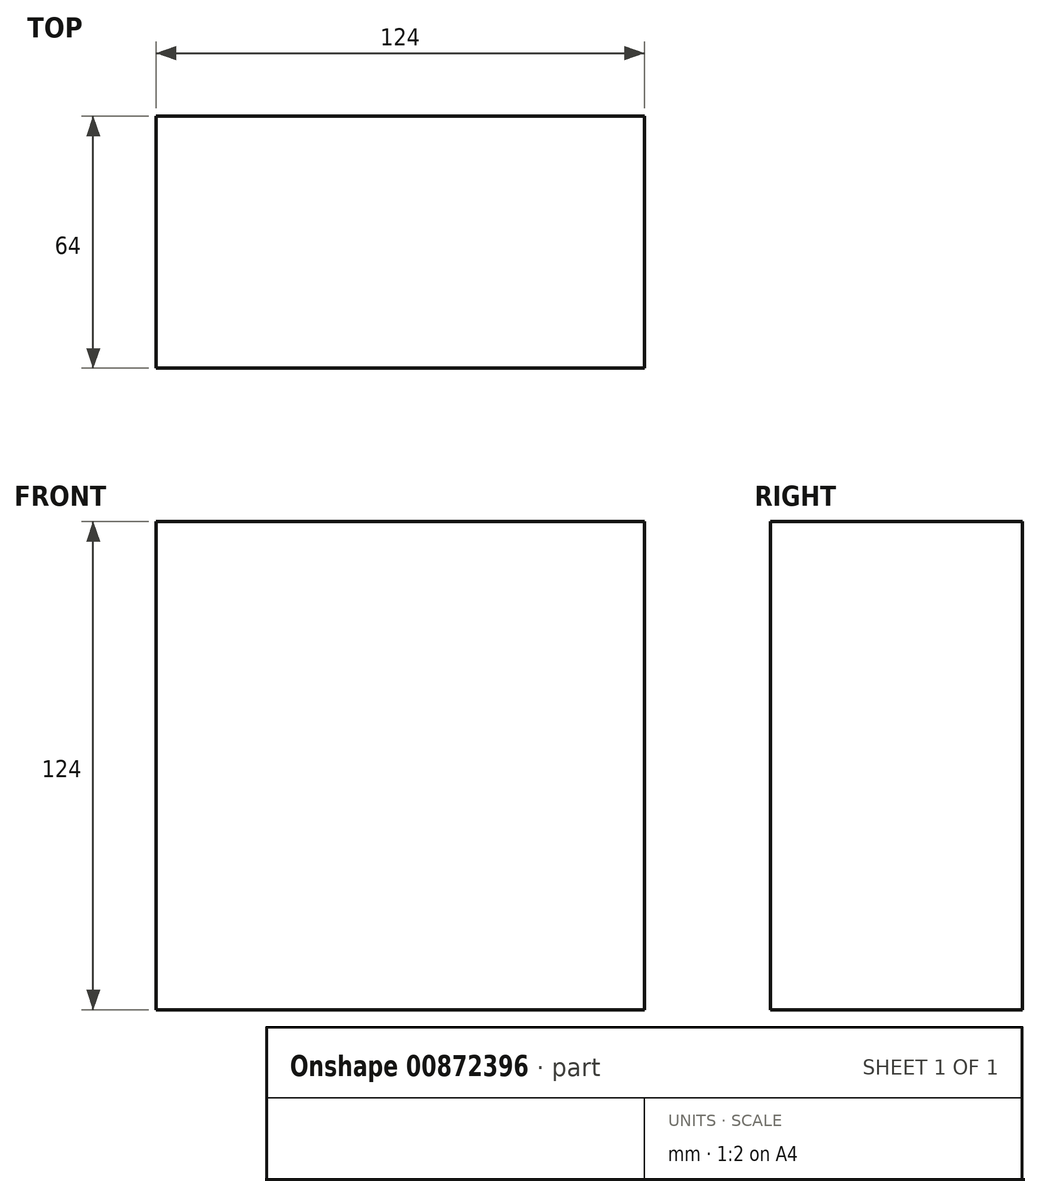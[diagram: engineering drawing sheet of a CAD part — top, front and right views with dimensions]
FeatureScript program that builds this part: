
annotation { "Feature Type Name" : "Feature", "Feature Type Description" : "" }
export const myFeature = defineFeature(function(context is Context, id is Id, definition is map)
    precondition{}
    {
        {
            var Q0;
            Q0=qCreatedBy(makeId("Top.planeOp"),FACE);
            var sketch = newSketch(context, id + "F0", { "sketchPlane" : qUnion([Q0])});
            skLineSegment(sketch, "E0.bottom", {"start": v(-62, 32) * mm, "end": v(62, 32) * mm});
            skLineSegment(sketch, "E0.top", {"start": v(-62, -32) * mm, "end": v(62, -32) * mm});
            skLineSegment(sketch, "E0.left", {"start": v(-62, 32) * mm, "end": v(-62, -32) * mm});
            skLineSegment(sketch, "E0.right", {"start": v(62, 32) * mm, "end": v(62, -32) * mm});
            skPoint(sketch, "E0.middle", {"position": v(0, 0) * mm});
            skSolve(sketch);
        }
        {
            var Q0;
            Q0 = qSketchRegion(id + "F0", true);
            extrude(context, id + "F1", {"entities" : qUnion([Q0]), "depth" : 124 * mm, "offsetDistance" : 25 * mm});
        }
    });
